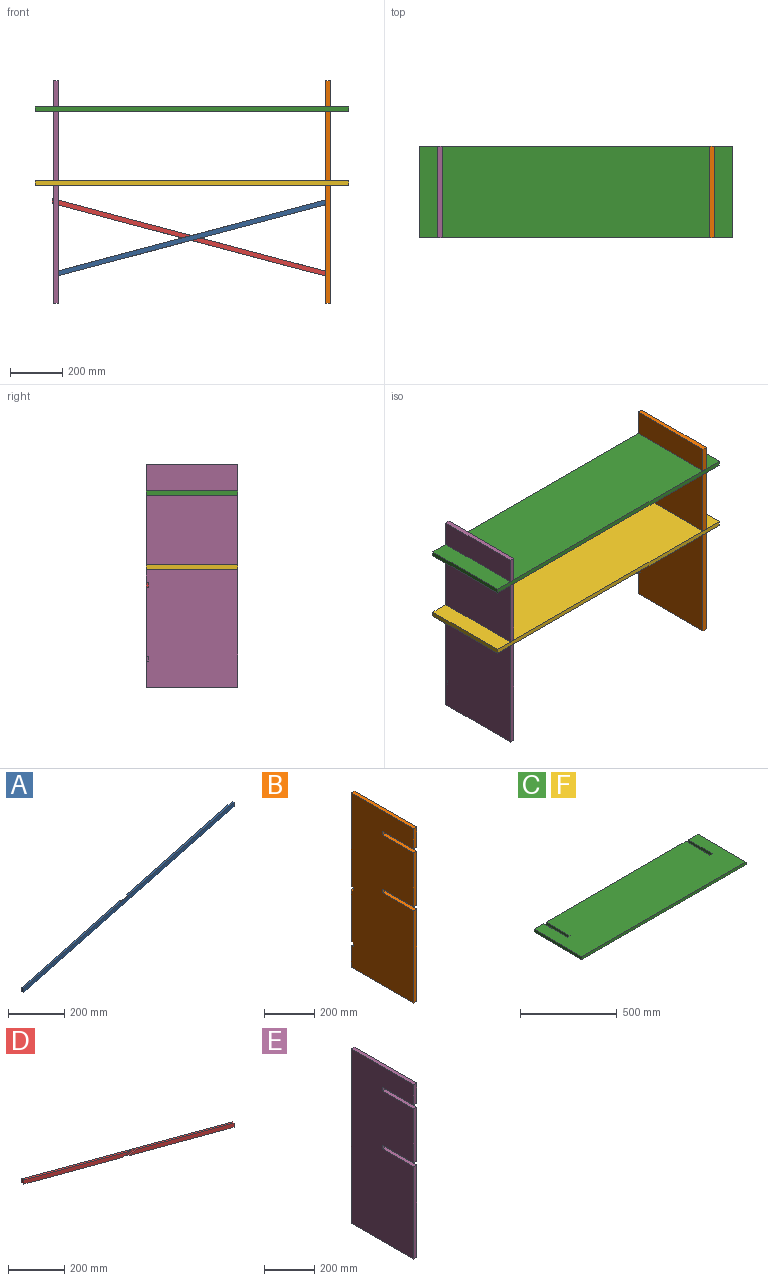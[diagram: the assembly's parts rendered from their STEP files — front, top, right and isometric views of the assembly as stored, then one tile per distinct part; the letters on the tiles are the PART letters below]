
ASSEMBLY  parts=6 mates=5
PART A: 10 faces, bbox 1058x10x300 mm
  f0: plane 531.51x150.71mm, normal (0,1,0), area 9575.2mm2, adj f2,f4,f5,f7
  f1: plane 526.47x149.36mm, normal (0,1,0), area 9481.2mm2, adj f2,f3,f5,f8
  f2: plane 1058x281.36mm, normal (0.26,0,-0.97), area 10767.3mm2, adj f0,f1,f3,f4,f6,f7,f8,f9
  f3: plane 18.63x10mm, normal (-1,0,0), area 186.3mm2, adj f1,f2,f5,f6
  f4: plane 18.63x10mm, normal (1,0,0), area 186.3mm2, adj f0,f2,f5,f6
  f5: plane 1058x281.36mm, normal (-0.26,0,0.97), area 10767.3mm2, adj f0,f1,f3,f4,f6,f7,f8,f9
  f6: plane 1058x299.99mm, normal (0,-1,0), area 19705.9mm2, adj f2,f3,f4,f5
  f7: plane 34.85x9.36mm, normal (-0.26,0,-0.97), area 180.4mm2, adj f0,f2,f5,f9
  f8: plane 34.85x9.36mm, normal (0.26,0,0.97), area 180.4mm2, adj f1,f2,f5,f9
  f9: plane 69.73x18.63mm, normal (0,1,0), area 649.6mm2, adj f2,f5,f7,f8
PART B: 22 faces, bbox 18x350x850 mm
  f0: plane 104.83x18mm, normal (0,1,0), area 1843.5mm2, adj f2,f12,f15,f19
  f1: plane 262.73x18mm, normal (0,1,0), area 4642.1mm2, adj f2,f15,f16,f20
  f2: plane 850x350mm, normal (1,0,0), area 290827.3mm2, adj f0,f1,f3,f4,f5,f6,f7,f8
  f3: plane 100x18mm, normal (0,-1,0), area 1800mm2, adj f2,f4,f14,f15
  f4: plane 175x18mm, normal (0,0,-1), area 3150mm2, adj f2,f3,f5,f15
  f5: plane 18x18mm, normal (0,-1,0), area 324mm2, adj f2,f4,f6,f15
  f6: plane 175x18mm, normal (0,0,1), area 3150mm2, adj f2,f5,f7,f15
  f7: plane 264x18mm, normal (0,-1,0), area 4752mm2, adj f2,f6,f8,f15
  f8: plane 175x18mm, normal (0,0,-1), area 3150mm2, adj f2,f7,f9,f15
  f9: plane 18x18mm, normal (0,-1,0), area 324mm2, adj f2,f8,f10,f15
  f10: plane 175x18mm, normal (0,0,1), area 3150mm2, adj f2,f9,f11,f15
  f11: plane 450x18mm, normal (0,-1,0), area 8100mm2, adj f2,f10,f12,f15
  f12: plane 350x18mm, normal (0,0,-1), area 6300mm2, adj f0,f2,f11,f15
  f13: plane 454.83x18mm, normal (0,1,0), area 8143.5mm2, adj f2,f14,f15,f17
  f14: plane 350x18mm, normal (0,0,1), area 6300mm2, adj f2,f3,f13,f15
  f15: plane 850x350mm, normal (-1,0,0), area 290827.3mm2, adj f0,f1,f3,f4,f5,f6,f7,f8
  f16: plane 18x10mm, normal (-0.26,0,0.97), area 186.4mm2, adj f1,f2,f15,f18
  f17: plane 18x10mm, normal (0.26,0,-0.97), area 186.4mm2, adj f2,f13,f15,f18
  f18: plane 23.47x18mm, normal (0,1,0), area 335.5mm2, adj f2,f15,f16,f17
  f19: plane 18x10mm, normal (0.26,0,0.97), area 186.4mm2, adj f0,f2,f15,f21
  f20: plane 18x10mm, normal (-0.26,0,-0.97), area 186.4mm2, adj f1,f2,f15,f21
  f21: plane 23.47x18mm, normal (0,1,0), area 335.5mm2, adj f2,f15,f19,f20
PART C: 14 faces, bbox 1198x350x18 mm
  f0: plane 18x18mm, normal (0,1,0), area 324mm2, adj f1,f11,f12,f13
  f1: plane 175x18mm, normal (1,0,0), area 3150mm2, adj f0,f2,f12,f13
  f2: plane 70x18mm, normal (0,1,0), area 1260mm2, adj f1,f3,f12,f13
  f3: plane 350x18mm, normal (-1,0,0), area 6300mm2, adj f2,f4,f12,f13
  f4: plane 1198x18mm, normal (0,-1,0), area 21564mm2, adj f3,f5,f12,f13
  f5: plane 350x18mm, normal (1,0,0), area 6300mm2, adj f4,f6,f12,f13
  f6: plane 70x18mm, normal (0,1,0), area 1260mm2, adj f5,f7,f12,f13
  f7: plane 175x18mm, normal (-1,0,0), area 3150mm2, adj f6,f8,f12,f13
  f8: plane 18x18mm, normal (0,1,0), area 324mm2, adj f7,f9,f12,f13
  f9: plane 175x18mm, normal (1,0,0), area 3150mm2, adj f8,f10,f12,f13
  f10: plane 1022x18mm, normal (0,1,0), area 18396mm2, adj f9,f11,f12,f13
  f11: plane 175x18mm, normal (-1,0,0), area 3150mm2, adj f0,f10,f12,f13
  f12: plane 1198x350mm, normal (0,0,1), area 413000mm2, adj f0,f1,f2,f3,f4,f5,f6,f7
  f13: plane 1198x350mm, normal (0,0,-1), area 413000mm2, adj f0,f1,f2,f3,f4,f5,f6,f7
PART D: 10 faces, bbox 1058x10x300 mm
  f0: plane 531.51x150.71mm, normal (0,-1,0), area 9575.2mm2, adj f1,f2,f3,f7
  f1: plane 1058x281.36mm, normal (-0.26,0,-0.97), area 10767.3mm2, adj f0,f3,f4,f5,f6,f7,f8,f9
  f2: plane 1058x281.36mm, normal (0.26,0,0.97), area 10767.3mm2, adj f0,f3,f4,f5,f6,f7,f8,f9
  f3: plane 18.63x10mm, normal (-1,0,0), area 186.3mm2, adj f0,f1,f2,f6
  f4: plane 18.63x10mm, normal (1,0,0), area 186.3mm2, adj f1,f2,f5,f6
  f5: plane 526.47x149.36mm, normal (0,-1,0), area 9481.2mm2, adj f1,f2,f4,f8
  f6: plane 1058x299.99mm, normal (0,1,0), area 19705.9mm2, adj f1,f2,f3,f4
  f7: plane 34.85x9.36mm, normal (0.26,0,-0.97), area 180.4mm2, adj f0,f1,f2,f9
  f8: plane 34.85x9.36mm, normal (-0.26,0,0.97), area 180.4mm2, adj f1,f2,f5,f9
  f9: plane 69.73x18.63mm, normal (0,-1,0), area 649.6mm2, adj f1,f2,f7,f8
PART E: 22 faces, bbox 18x350x850 mm
  f0: plane 850x18mm, normal (0,1,0), area 14964.5mm2, adj f1,f2,f3,f13,f14,f15,f16,f18
  f1: plane 850x350mm, normal (1,0,0), area 290827.3mm2, adj f0,f2,f3,f4,f5,f6,f7,f8
  f2: plane 350x18mm, normal (0,0,-1), area 6300mm2, adj f0,f1,f12,f13
  f3: plane 350x18mm, normal (0,0,1), area 6300mm2, adj f0,f1,f4,f13
  f4: plane 100x18mm, normal (0,-1,0), area 1800mm2, adj f1,f3,f5,f13
  f5: plane 175x18mm, normal (0,0,-1), area 3150mm2, adj f1,f4,f6,f13
  f6: plane 18x18mm, normal (0,-1,0), area 324mm2, adj f1,f5,f7,f13
  f7: plane 175x18mm, normal (0,0,1), area 3150mm2, adj f1,f6,f8,f13
  f8: plane 264x18mm, normal (0,-1,0), area 4752mm2, adj f1,f7,f9,f13
  f9: plane 175x18mm, normal (0,0,-1), area 3150mm2, adj f1,f8,f10,f13
  f10: plane 18x18mm, normal (0,-1,0), area 324mm2, adj f1,f9,f11,f13
  f11: plane 175x18mm, normal (0,0,1), area 3150mm2, adj f1,f10,f12,f13
  f12: plane 450x18mm, normal (0,-1,0), area 8100mm2, adj f1,f2,f11,f13
  f13: plane 850x350mm, normal (-1,0,0), area 291200mm2, adj f0,f2,f3,f4,f5,f6,f7,f8
  f14: plane 10x9mm, normal (0.26,0,0.97), area 93.2mm2, adj f0,f1,f15,f17
  f15: plane 18.64x10mm, normal (1,0,0), area 186.4mm2, adj f0,f14,f16,f17
  f16: plane 10x9mm, normal (-0.26,0,-0.97), area 93.2mm2, adj f0,f1,f15,f17
  f17: plane 21.05x9mm, normal (0,1,0), area 167.7mm2, adj f1,f14,f15,f16
  f18: plane 10x9mm, normal (-0.26,0,0.97), area 93.2mm2, adj f0,f1,f19,f21
  f19: plane 18.64x10mm, normal (1,0,0), area 186.4mm2, adj f0,f18,f20,f21
  f20: plane 10x9mm, normal (0.26,0,-0.97), area 93.2mm2, adj f0,f1,f19,f21
  f21: plane 21.05x9mm, normal (0,1,0), area 167.7mm2, adj f1,f18,f19,f20
PART F: same geometry as C
PLACE A t=(-2162.24,-361.36,-1.12)mm
PLACE B t=(-701.94,-361.36,-516.28)mm
PLACE C t=(-1811.94,-711.36,215.72)mm
PLACE D t=(-1230.38,-361.36,-266.66)mm
PLACE E t=(-702.94,-361.36,-516.28)mm
PLACE F t=(-1811.94,-711.36,-66.28)mm
MATE fastened A.f9 <-> D.f9  axis (0,1,0) through (-1215.46,-366.36,-266.88)mm
MATE fastened C.f0 <-> E.f6  axis (0,1,0) through (-1732.94,-536.36,224.72)mm
MATE fastened E.f10 <-> F.f0  axis (0,-1,0) through (-1732.94,-536.36,-57.28)mm
MATE fastened C.f8 <-> B.f5  axis (0,1,0) through (-692.94,-536.36,224.72)mm
MATE fastened B.f18 <-> A.f6  axis (0,1,0) through (-692.94,-371.36,-128.01)mm
